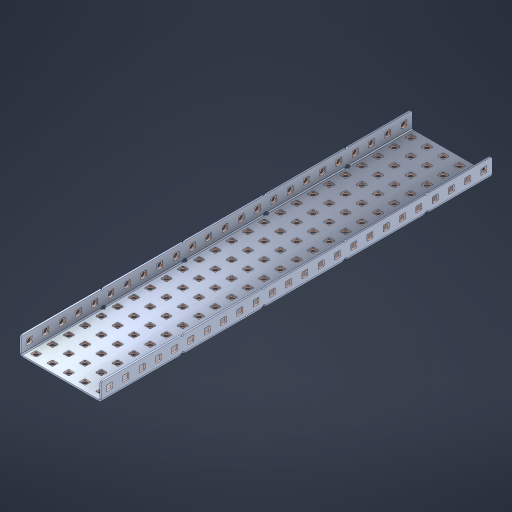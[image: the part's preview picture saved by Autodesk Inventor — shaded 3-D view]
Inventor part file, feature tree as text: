
AUTODESK INVENTOR PART (.ipt)
format: ipt  version: 2023 (Build 270158000, 158)  size: 1,878,528 bytes
history: native  units: in
note: dims shown in document units (in); Inventor stores cm internally (conversion verified against a paired STEP export)
features: other x173, extrude x167, sheet_metal_op x10, sketch x8, mirror x1, pattern_linear x1, chamfer x1
ambient origin geometry x8: Origin, YZ Plane, XZ Plane, XY Plane, X Axis, Y Axis, Z Axis, Center Point
bodies: Solid1 (feature_tree), Body (feature_tree)
feature tree (361):
  other  "Flange Pattern Plane"
  sheet_metal_op  "Flange Pattern"
  sheet_metal_op  "Body Pattern"
  other  "Arc Length"
  mirror  "Notch Mirror"
  pattern_linear  "Notch Pattern"  Spacing1=0.1875in  [1 undecoded]
  chamfer  "End Chamfer"
  extrude  "Half Cut"  Depth=0.0469in
  sketch  "Sketch1"  dims[d0=2.5in]
  other  "Plate1"
  sketch  "Sketch2"  dims[d1=12.0in]
  other  "Plate2"
  sheet_metal_op  "Bend1"
  sheet_metal_op  "Corner1"
  sketch  "Sketch3"  dims[d2=0.0469in]
  other  "Flange Pattern Sketch"
  sketch  "Sketch7"  dims[d3=0.0469in]
  other  "Srf1"
  other  "Srf2"
  sketch  "Sketch8"  dims[d4=0.0234in]
  sketch  "Sketch9"  dims[d5=0.0938in]
  other  "Srf91"
  sheet_metal_op  "Body Pattern Sketch"
  other  "Srf92"
  sketch  "Sketch13"  dims[d6=0.0469in]
  sketch  "Sketch14"  dims[d7=0.5in d8=90.0deg d9=0.0312in d10=0.1875in d11=0.0469in d12=0.0469in d16=0.182in d17=0.02in d18=0.0469in d19=0.0in d20=0.25in d21=0.25in d46=0.172in d47=1.0in d48=0.0in d49=0.182in d50=0.02in d51=0.25in d52=0.25in d53=0.0469in d54=0.0in d55=0.172in d56=1.0in d57=0.0in d60=9.4488in d62=0.5in d63=1.9685in d65=0.5in d85=0.1227in d86=0.1659in d88=0.04in d89=0.0469in d90=0.0in d91=0.04in d92=0.0491in d95=2.5in d96=0.04in d97=0.25in d98=45.0deg d101=0.0in d102=2.497in d131=2.5in d132=9.4488in d134=0.5in d139=0.5in]
  other  "Srf856"
  other  "Srf1310"
  other  "Srf1311"
  other  "Srf1312"
  other  "Srf1376"
  other  "Srf1377"
  other  "Srf1728"
  other  "Srf1755"
  other  "Srf1878"
  other  "Srf1879"
  other  "Srf1880"
  other  "Srf1881"
  other  "Srf1882"
  other  "Srf1883"
  other  "Srf1884"
  other  "Srf1885"
  other  "Srf1886"
  other  "Srf1887"
  other  "Srf1888"
  other  "Srf1889"
  other  "Srf1890"
  other  "Srf1891"
  other  "Srf1892"
  other  "Srf1893"
  other  "Srf1894"
  other  "Srf1895"
  other  "Srf1896"
  other  "Srf1897"
  other  "Srf1898"
  other  "Srf1899"
  other  "Srf1900"
  other  "Srf1901"
  other  "Srf1902"
  other  "Srf1903"
  other  "Srf1904"
  other  "Srf1905"
  other  "Srf1906"
  other  "Srf1942"
  other  "Srf1943"
  other  "Srf1944"
  other  "Srf1945"
  other  "Srf1946"
  other  "Srf1947"
  other  "Srf1948"
  other  "Srf1949"
  other  "Srf1950"
  other  "Srf1951"
  other  "Srf1952"
  other  "Srf1953"
  other  "Srf1954"
  other  "Srf1955"
  other  "Srf1956"
  other  "Srf1957"
  other  "Srf1958"
  other  "Srf1959"
  other  "Srf1960"
  other  "Srf1961"
  other  "Srf1962"
  other  "Srf1963"
  other  "Srf1964"
  other  "Srf1965"
  other  "Srf1966"
  other  "Srf1967"
  other  "Srf1968"
  other  "Srf1969"
  other  "Srf1970"
  other  "Srf2111"
  other  "Srf2112"
  other  "Srf2113"
  other  "Srf2114"
  other  "Srf2115"
  other  "Srf2116"
  other  "Srf2117"
  other  "Srf2118"
  other  "Srf2119"
  other  "Srf2120"
  other  "Srf2121"
  other  "Srf2122"
  other  "Srf2123"
  other  "Srf2146"
  other  "Srf2147"
  other  "Srf2148"
  other  "Srf2149"
  other  "Srf2150"
  other  "Srf2151"
  other  "Srf2152"
  other  "Srf2153"
  other  "Srf2154"
  other  "Srf2155"
  other  "Srf2156"
  other  "Srf2157"
  other  "Srf2158"
  other  "Srf2159"
  other  "Srf2160"
  other  "Srf2161"
  other  "Srf2162"
  other  "Srf2163"
  other  "Srf2164"
  other  "Srf2165"
  other  "Srf2166"
  other  "Srf2167"
  other  "Srf2168"
  other  "Srf2169"
  other  "Srf2170"
  other  "Srf2171"
  other  "Srf2172"
  other  "Srf2173"
  other  "Srf2174"
  other  "Srf2175"
  other  "Srf2176"
  other  "Srf2177"
  other  "Srf2178"
  other  "Srf2179"
  other  "Srf2180"
  other  "Srf2181"
  other  "Srf2182"
  other  "Srf2183"
  other  "Srf2184"
  other  "Srf2185"
  other  "Srf2186"
  other  "Srf2187"
  other  "Srf2188"
  other  "Srf2189"
  other  "Srf2190"
  other  "Srf2191"
  other  "Srf2192"
  other  "Srf2193"
  other  "Srf2194"
  other  "Srf2195"
  other  "Srf2196"
  other  "Srf2197"
  other  "Srf2198"
  other  "Srf2199"
  other  "Srf2200"
  other  "Srf2201"
  other  "Srf2202"
  other  "Srf2203"
  other  "Srf2204"
  other  "Srf2205"
  other  "Srf2206"
  other  "Srf2207"
  other  "Srf2208"
  other  "Srf2209"
  other  "Srf2210"
  other  "Srf2211"
  other  "Srf2212"
  other  "Srf2213"
  other  "Srf2214"
  other  "Srf2215"
  other  "Srf2216"
  other  "Srf2217"
  other  "Srf2218"
  other  "Srf2219"
  other  "Srf2220"
  other  "Srf2221"
  other  "Srf2222"
  other  "Srf2223"
  other  "Srf2224"
  other  "Srf2225"
  other  "Srf2226"
  other  "Srf2227"
  other  "Srf2228"
  other  "Srf2229"
  other  "Srf2230"
  sheet_metal_op  "Flange Stamp"
  sheet_metal_op  "Flange Circle"
  sheet_metal_op  "Body Stamp"
  sheet_metal_op  "Body Circle"
  sheet_metal_op  "Notch"
  extrude  "ExtrusionSrf2"  Depth=0.0469in
  extrude  "ExtrusionSrf92"  Depth=2.5in
  extrude  "ExtrusionSrf856"  Depth=0.02in
  extrude  "ExtrusionSrf1310"  Depth=0.0469in
  extrude  "ExtrusionSrf1311"  TaperAngle=0.0deg  [1 undecoded]
  extrude  "ExtrusionSrf1312"  Depth=0.25in
  extrude  "ExtrusionSrf1376"  Depth=0.25in
  extrude  "ExtrusionSrf1377"  Depth=2.5in
  extrude  "ExtrusionSrf1728"  Depth=2.5in TaperAngle=0.0deg
  extrude  "ExtrusionSrf1755"  Depth=2.5in
  extrude  "ExtrusionSrf1878"  Depth=0.02in
  extrude  "ExtrusionSrf1879"  Depth=0.25in
  extrude  "ExtrusionSrf1880"  Depth=0.25in
  extrude  "ExtrusionSrf1881"  Depth=0.0469in
  extrude  "ExtrusionSrf1882"  TaperAngle=0.0deg  [1 undecoded]
  extrude  "ExtrusionSrf1883"  Depth=2.5in
  extrude  "ExtrusionSrf1884"  Depth=2.5in TaperAngle=0.0deg
  extrude  "ExtrusionSrf1885"  Depth=2.5in
  extrude  "ExtrusionSrf1886"  Depth=2.5in
  extrude  "ExtrusionSrf1887"  Depth=2.5in
  extrude  "ExtrusionSrf1888"  Depth=2.5in
  extrude  "ExtrusionSrf1889"  Depth=2.5in
  extrude  "ExtrusionSrf1890"  Depth=0.0469in
  extrude  "ExtrusionSrf1891"  TaperAngle=0.0deg  [1 undecoded]
  extrude  "ExtrusionSrf1892"  Depth=2.5in
  extrude  "ExtrusionSrf1893"  Depth=2.5in
  extrude  "ExtrusionSrf1894"  Depth=2.5in
  extrude  "ExtrusionSrf1895"  Depth=0.25in TaperAngle=45.0deg
  extrude  "ExtrusionSrf1896"  TaperAngle=0.0deg  [1 undecoded]
  extrude  "ExtrusionSrf1897"  Depth=2.5in
  extrude  "ExtrusionSrf1898"  Depth=2.5in
  extrude  "ExtrusionSrf1899"  Depth=2.5in
  extrude  "ExtrusionSrf1900"  Depth=2.5in
  extrude  "ExtrusionSrf1901"  Depth=2.5in
  extrude  "ExtrusionSrf1902"  [1 undecoded]
  extrude  "ExtrusionSrf1903"  [1 undecoded]
  extrude  "ExtrusionSrf1904"  [1 undecoded]
  extrude  "ExtrusionSrf1905"  [1 undecoded]
  extrude  "ExtrusionSrf1906"  [1 undecoded]
  extrude  "ExtrusionSrf1942"  [1 undecoded]
  extrude  "ExtrusionSrf1943"  [1 undecoded]
  extrude  "ExtrusionSrf1944"  [1 undecoded]
  extrude  "ExtrusionSrf1945"  [1 undecoded]
  extrude  "ExtrusionSrf1946"  [1 undecoded]
  extrude  "ExtrusionSrf1947"  [1 undecoded]
  extrude  "ExtrusionSrf1948"  [1 undecoded]
  extrude  "ExtrusionSrf1949"  [1 undecoded]
  extrude  "ExtrusionSrf1950"  [1 undecoded]
  extrude  "ExtrusionSrf1951"  [1 undecoded]
  extrude  "ExtrusionSrf1952"  [1 undecoded]
  extrude  "ExtrusionSrf1953"  [1 undecoded]
  extrude  "ExtrusionSrf1954"  [1 undecoded]
  extrude  "ExtrusionSrf1955"  [1 undecoded]
  extrude  "ExtrusionSrf1956"  [1 undecoded]
  extrude  "ExtrusionSrf1957"  [1 undecoded]
  extrude  "ExtrusionSrf1958"  [1 undecoded]
  extrude  "ExtrusionSrf1959"  [1 undecoded]
  extrude  "ExtrusionSrf1960"  [1 undecoded]
  extrude  "ExtrusionSrf1961"  [1 undecoded]
  extrude  "ExtrusionSrf1962"  [1 undecoded]
  extrude  "ExtrusionSrf1963"  [1 undecoded]
  extrude  "ExtrusionSrf1964"  [1 undecoded]
  extrude  "ExtrusionSrf1965"  [1 undecoded]
  extrude  "ExtrusionSrf1966"  [1 undecoded]
  extrude  "ExtrusionSrf1967"  [1 undecoded]
  extrude  "ExtrusionSrf1968"  [1 undecoded]
  extrude  "ExtrusionSrf1969"  [1 undecoded]
  extrude  "ExtrusionSrf1970"  [1 undecoded]
  extrude  "ExtrusionSrf2111"  [1 undecoded]
  extrude  "ExtrusionSrf2112"  [1 undecoded]
  extrude  "ExtrusionSrf2113"  [1 undecoded]
  extrude  "ExtrusionSrf2114"  [1 undecoded]
  extrude  "ExtrusionSrf2115"  [1 undecoded]
  extrude  "ExtrusionSrf2116"  [1 undecoded]
  extrude  "ExtrusionSrf2117"  [1 undecoded]
  extrude  "ExtrusionSrf2118"  [1 undecoded]
  extrude  "ExtrusionSrf2119"  [1 undecoded]
  extrude  "ExtrusionSrf2120"  [1 undecoded]
  extrude  "ExtrusionSrf2121"  [1 undecoded]
  extrude  "ExtrusionSrf2122"  [1 undecoded]
  extrude  "ExtrusionSrf2123"  [1 undecoded]
  extrude  "ExtrusionSrf2146"  [1 undecoded]
  extrude  "ExtrusionSrf2147"  [1 undecoded]
  extrude  "ExtrusionSrf2148"  [1 undecoded]
  extrude  "ExtrusionSrf2149"  [1 undecoded]
  extrude  "ExtrusionSrf2150"  [1 undecoded]
  extrude  "ExtrusionSrf2151"  [1 undecoded]
  extrude  "ExtrusionSrf2152"  [1 undecoded]
  extrude  "ExtrusionSrf2153"  [1 undecoded]
  extrude  "ExtrusionSrf2154"  [1 undecoded]
  extrude  "ExtrusionSrf2155"  [1 undecoded]
  extrude  "ExtrusionSrf2156"  [1 undecoded]
  extrude  "ExtrusionSrf2157"  [1 undecoded]
  extrude  "ExtrusionSrf2158"  [1 undecoded]
  extrude  "ExtrusionSrf2159"  [1 undecoded]
  extrude  "ExtrusionSrf2160"  [1 undecoded]
  extrude  "ExtrusionSrf2161"  [1 undecoded]
  extrude  "ExtrusionSrf2162"  [1 undecoded]
  extrude  "ExtrusionSrf2163"  [1 undecoded]
  extrude  "ExtrusionSrf2164"  [1 undecoded]
  extrude  "ExtrusionSrf2165"  [1 undecoded]
  extrude  "ExtrusionSrf2166"  [1 undecoded]
  extrude  "ExtrusionSrf2167"  [1 undecoded]
  extrude  "ExtrusionSrf2168"  [1 undecoded]
  extrude  "ExtrusionSrf2169"  [1 undecoded]
  extrude  "ExtrusionSrf2170"  [1 undecoded]
  extrude  "ExtrusionSrf2171"  [1 undecoded]
  extrude  "ExtrusionSrf2172"  [1 undecoded]
  extrude  "ExtrusionSrf2173"  [1 undecoded]
  extrude  "ExtrusionSrf2174"  [1 undecoded]
  extrude  "ExtrusionSrf2175"  [1 undecoded]
  extrude  "ExtrusionSrf2176"  [1 undecoded]
  extrude  "ExtrusionSrf2177"  [1 undecoded]
  extrude  "ExtrusionSrf2178"  [1 undecoded]
  extrude  "ExtrusionSrf2179"  [1 undecoded]
  extrude  "ExtrusionSrf2180"  [1 undecoded]
  extrude  "ExtrusionSrf2181"  [1 undecoded]
  extrude  "ExtrusionSrf2182"  [1 undecoded]
  extrude  "ExtrusionSrf2183"  [1 undecoded]
  extrude  "ExtrusionSrf2184"  [1 undecoded]
  extrude  "ExtrusionSrf2185"  [1 undecoded]
  extrude  "ExtrusionSrf2186"  [1 undecoded]
  extrude  "ExtrusionSrf2187"  [1 undecoded]
  extrude  "ExtrusionSrf2188"  [1 undecoded]
  extrude  "ExtrusionSrf2189"  [1 undecoded]
  extrude  "ExtrusionSrf2190"  [1 undecoded]
  extrude  "ExtrusionSrf2191"  [1 undecoded]
  extrude  "ExtrusionSrf2192"  [1 undecoded]
  extrude  "ExtrusionSrf2193"  [1 undecoded]
  extrude  "ExtrusionSrf2194"  [1 undecoded]
  extrude  "ExtrusionSrf2195"  [1 undecoded]
  extrude  "ExtrusionSrf2196"  [1 undecoded]
  extrude  "ExtrusionSrf2197"  [1 undecoded]
  extrude  "ExtrusionSrf2198"  [1 undecoded]
  extrude  "ExtrusionSrf2199"  [1 undecoded]
  extrude  "ExtrusionSrf2200"  [1 undecoded]
  extrude  "ExtrusionSrf2201"  [1 undecoded]
  extrude  "ExtrusionSrf2202"  [1 undecoded]
  extrude  "ExtrusionSrf2203"  [1 undecoded]
  extrude  "ExtrusionSrf2204"  [1 undecoded]
  extrude  "ExtrusionSrf2205"  [1 undecoded]
  extrude  "ExtrusionSrf2206"  [1 undecoded]
  extrude  "ExtrusionSrf2207"  [1 undecoded]
  extrude  "ExtrusionSrf2208"  [1 undecoded]
  extrude  "ExtrusionSrf2209"  [1 undecoded]
  extrude  "ExtrusionSrf2210"  [1 undecoded]
  extrude  "ExtrusionSrf2211"  [1 undecoded]
  extrude  "ExtrusionSrf2212"  [1 undecoded]
  extrude  "ExtrusionSrf2213"  [1 undecoded]
  extrude  "ExtrusionSrf2214"  [1 undecoded]
  extrude  "ExtrusionSrf2215"  [1 undecoded]
  extrude  "ExtrusionSrf2216"  [1 undecoded]
  extrude  "ExtrusionSrf2217"  [1 undecoded]
  extrude  "ExtrusionSrf2218"  [1 undecoded]
  extrude  "ExtrusionSrf2219"  [1 undecoded]
  extrude  "ExtrusionSrf2220"  [1 undecoded]
  extrude  "ExtrusionSrf2221"  [1 undecoded]
  extrude  "ExtrusionSrf2222"  [1 undecoded]
  extrude  "ExtrusionSrf2223"  [1 undecoded]
  extrude  "ExtrusionSrf2224"  [1 undecoded]
  extrude  "ExtrusionSrf2225"  [1 undecoded]
  extrude  "ExtrusionSrf2226"  [1 undecoded]
  extrude  "ExtrusionSrf2227"  [1 undecoded]
  extrude  "ExtrusionSrf2228"  [1 undecoded]
  extrude  "ExtrusionSrf2229"  [1 undecoded]
  extrude  "ExtrusionSrf2230"  [1 undecoded]
note: 137 required parameter values undecoded (feature->parameter linkage not recoverable at this tier; creation-order binding heuristic only, values carry confidence <= 0.55)
